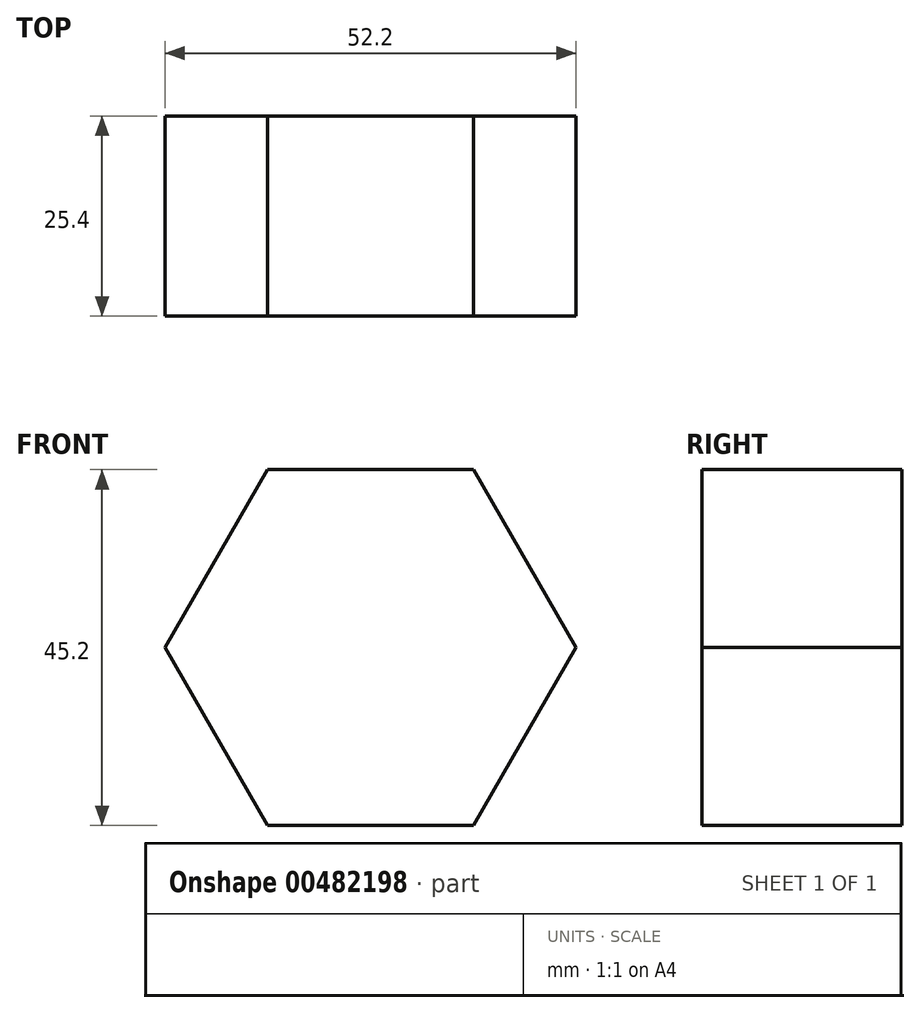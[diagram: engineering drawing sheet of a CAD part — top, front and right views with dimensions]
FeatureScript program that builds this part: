
annotation { "Feature Type Name" : "Feature", "Feature Type Description" : "" }
export const myFeature = defineFeature(function(context is Context, id is Id, definition is map)
    precondition{}
    {
        {
            var Q0;
            Q0=qCreatedBy(makeId("Front.planeOp"),FACE);
            var sketch = newSketch(context, id + "F0", { "sketchPlane" : qUnion([Q0])});
            skCircle(sketch, "E0.cCircle", {"center": v(0, 0) * mm, "radius": 26.1 * mm, "construction": true});
            skLineSegment(sketch, "E0.0", {"start": v(26.1, 0) * mm, "end": v(13.05, -22.6) * mm});
            skLineSegment(sketch, "E0.1", {"start": v(13.05, -22.6) * mm, "end": v(-13.05, -22.6) * mm});
            skLineSegment(sketch, "E0.2", {"start": v(-13.05, -22.6) * mm, "end": v(-26.1, 0) * mm});
            skLineSegment(sketch, "E0.3", {"start": v(-26.1, 0) * mm, "end": v(-13.05, 22.6) * mm});
            skLineSegment(sketch, "E0.4", {"start": v(-13.05, 22.6) * mm, "end": v(13.05, 22.6) * mm});
            skLineSegment(sketch, "E0.5", {"start": v(13.05, 22.6) * mm, "end": v(26.1, 0) * mm});
            skSolve(sketch);
        }
        {
            var Q0;
            Q0=makeQuery(id+"F0.imprint","IMPRINT",FACE,{"disambiguationData":[TD([[makeQuery(id+"F0.imprint","IMPRINT",EDGE,{"derivedFrom":sQuery(id+"F0.wireOp",EDGE,"E0.0")}),-1.0]])]});
            extrude(context, id + "F1", {"entities" : qUnion([Q0]), "depth" : 25.4 * mm, "offsetDistance" : 25.4 * mm});
        }
    });
